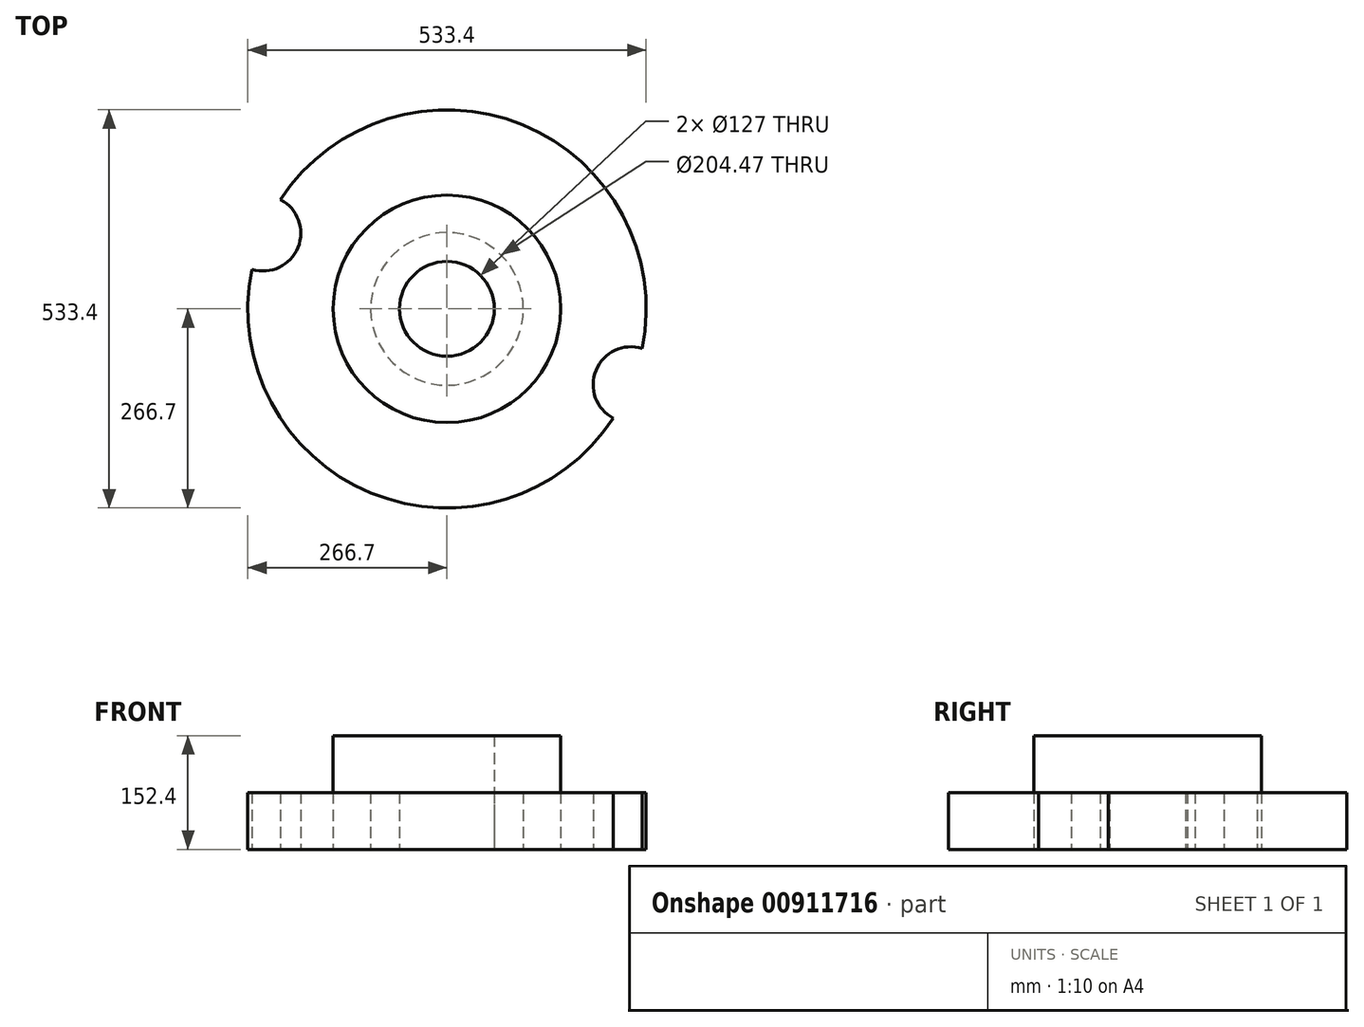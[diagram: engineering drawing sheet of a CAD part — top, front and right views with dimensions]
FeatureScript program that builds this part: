
annotation { "Feature Type Name" : "Feature", "Feature Type Description" : "" }
export const myFeature = defineFeature(function(context is Context, id is Id, definition is map)
    precondition{}
    {
        {
            var Q0;
            Q0=qCreatedBy(makeId("Top.planeOp"),FACE);
            var sketch = newSketch(context, id + "F0", { "sketchPlane" : qUnion([Q0])});
            skCircle(sketch, "E0", {"center": v(0, 0) * mm, "radius": 63.5 * mm});
            skCircle(sketch, "E1", {"center": v(0, 0) * mm, "radius": 152.4 * mm});
            skSolve(sketch);
        }
        {
            var Q0;
            Q0=makeQuery(id+"F0.imprint","IMPRINT",FACE,{"disambiguationData":[TD([[makeQuery(id+"F0.imprint","IMPRINT",EDGE,{"derivedFrom":sQuery(id+"F0.wireOp",EDGE,"E0")}),-1.0]])]});
            extrude(context, id + "F1", {"entities" : qUnion([Q0]), "depth" : 152.4 * mm, "offsetDistance" : 25.4 * mm});
        }
        {
            var Q0;
            Q0=qCreatedBy(makeId("Top.planeOp"),FACE);
            var sketch = newSketch(context, id + "F2", { "sketchPlane" : qUnion([Q0])});
            skCircle(sketch, "E2", {"center": v(0, 0) * mm, "radius": 102.24 * mm});
            skCircle(sketch, "E3", {"center": v(0, 0) * mm, "radius": 266.7 * mm});
            skCircle(sketch, "E4", {"center": v(-246.6, 101.58) * mm, "radius": 50.8 * mm});
            skCircle(sketch, "E5", {"center": v(246.6, -101.58) * mm, "radius": 50.8 * mm});
            skLineSegment(sketch, "E6", {"start": v(-246.6, 101.58) * mm, "end": v(246.6, -101.58) * mm, "construction": true});
            skSolve(sketch);
        }
        {
            var Q0;
            Q0=makeQuery(id+"F2.imprint","IMPRINT",FACE,{"disambiguationData":[TD([[makeQuery(id+"F2.imprint","IMPRINT",EDGE,{"derivedFrom":sQuery(id+"F2.wireOp",EDGE,"E2")}),-1.0]])]});
            var Q1;
            Q1 = qSketchRegion(id + "F0", true);
            extrude(context, id + "F3", {"entities" : qUnion([Q0, Q1]), "depth" : 76.2 * mm, "offsetDistance" : 25.4 * mm});
        }
    });
